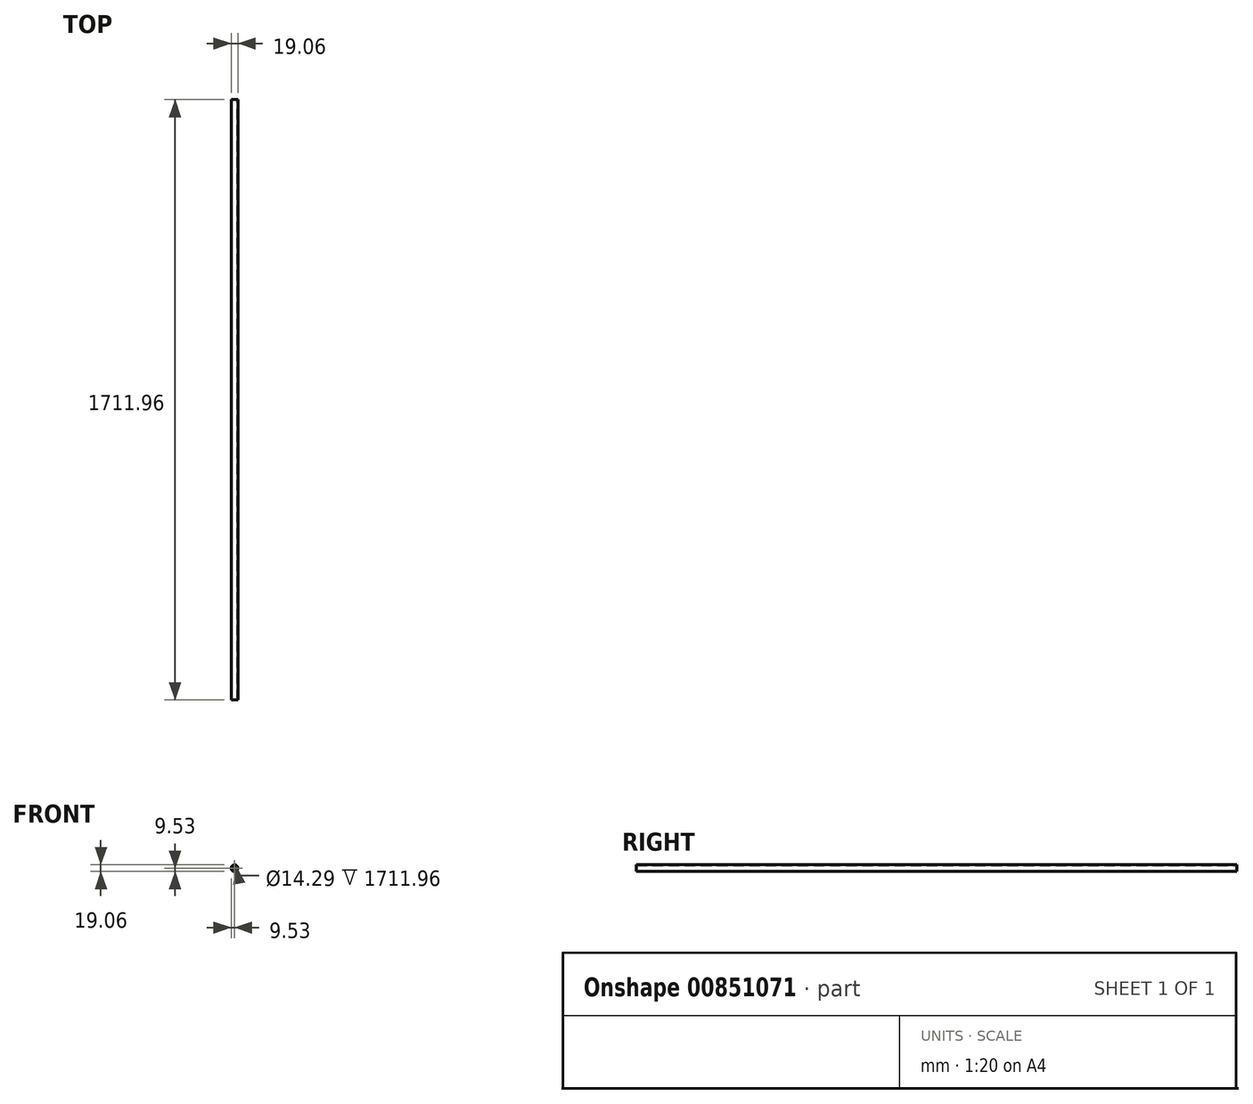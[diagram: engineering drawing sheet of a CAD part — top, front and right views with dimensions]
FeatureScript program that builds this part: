
annotation { "Feature Type Name" : "Feature", "Feature Type Description" : "" }
export const myFeature = defineFeature(function(context is Context, id is Id, definition is map)
    precondition{}
    {
        {
            var Q0;
            Q0=qCreatedBy(makeId("Front.planeOp"),FACE);
            var sketch = newSketch(context, id + "F0", { "sketchPlane" : qUnion([Q0])});
            skCircle(sketch, "E0", {"center": v(0, 0) * mm, "radius": 7.14 * mm});
            skCircle(sketch, "E1", {"center": v(0, 0) * mm, "radius": 9.53 * mm});
            skSolve(sketch);
        }
        {
            var Q0;
            Q0=makeQuery(id+"F0.imprint","IMPRINT",FACE,{"disambiguationData":[TD([[makeQuery(id+"F0.imprint","IMPRINT",EDGE,{"derivedFrom":sQuery(id+"F0.wireOp",EDGE,"E0")}),-1.0]])]});
            var Q1;
            Q1 = qSketchRegion(id + "F2", true);
            extrude(context, id + "F1", {"entities" : qUnion([Q0, Q1]), "depth" : 855.98 * mm, "offsetDistance" : 25.4 * mm, "hasSecondDirection" : true, "secondDirectionOppositeDirection" : true, "secondDirectionDepth" : 855.98 * mm});
        }
    });
